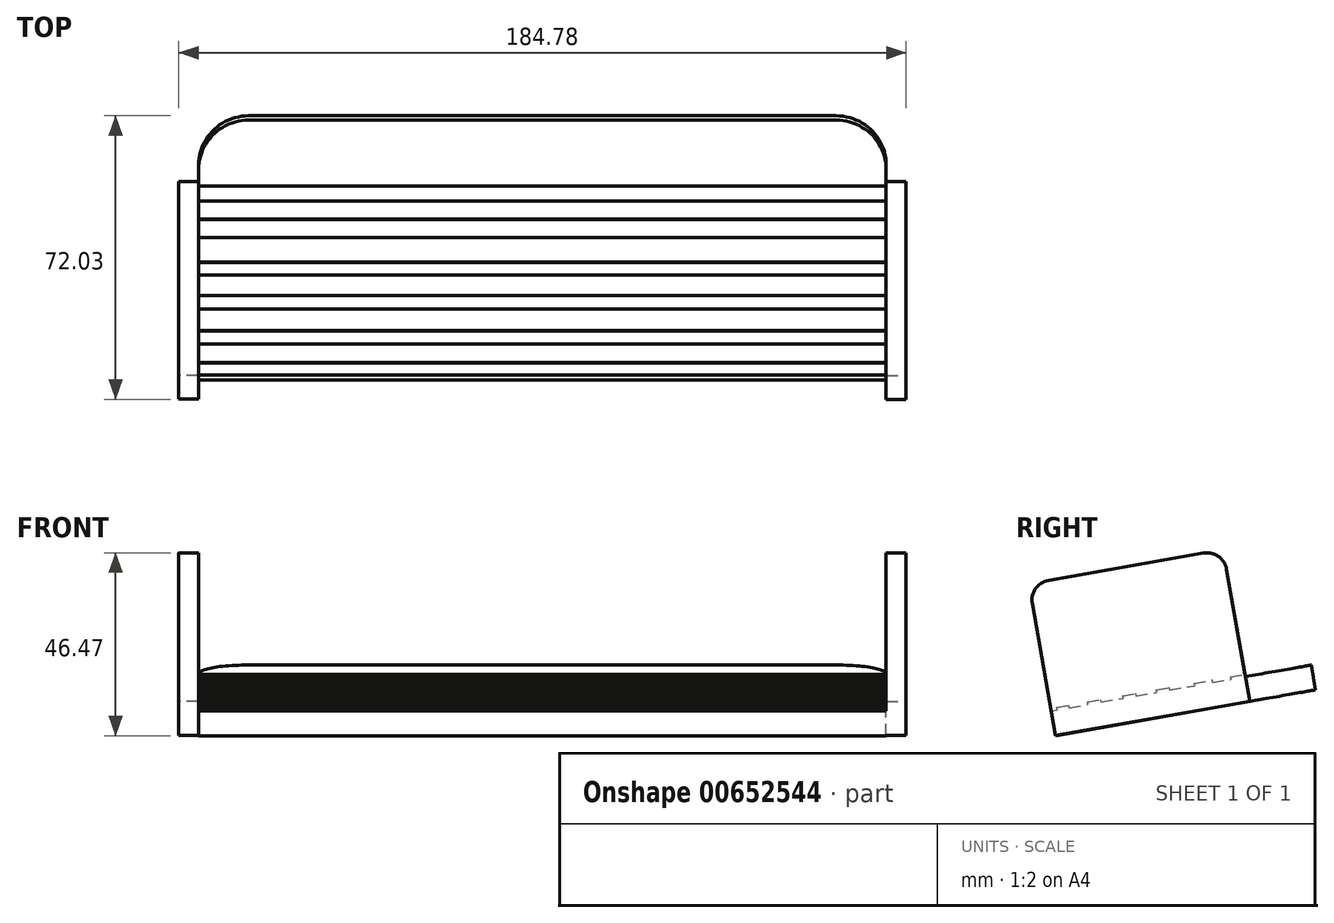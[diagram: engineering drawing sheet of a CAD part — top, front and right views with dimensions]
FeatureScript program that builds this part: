
annotation { "Feature Type Name" : "Feature", "Feature Type Description" : "" }
export const myFeature = defineFeature(function(context is Context, id is Id, definition is map)
    precondition{}
    {
        {
            var Q0;
            Q0=qCreatedBy(makeId("Front.planeOp"),FACE);
            var sketch = newSketch(context, id + "F0", { "sketchPlane" : qUnion([Q0])});
            skLineSegment(sketch, "E0.bottom", {"start": v(-82.9, 3.26) * mm, "end": v(91.78, 3.26) * mm});
            skLineSegment(sketch, "E0.top", {"start": v(-82.9, -3.13) * mm, "end": v(91.78, -3.13) * mm});
            skLineSegment(sketch, "E0.left", {"start": v(-82.9, 3.26) * mm, "end": v(-82.9, -3.13) * mm});
            skLineSegment(sketch, "E0.right", {"start": v(91.78, 3.26) * mm, "end": v(91.78, -3.13) * mm});
            skSolve(sketch);
        }
        {
            var Q0;
            Q0 = qSketchRegion(id + "F0", true);
            var Q1;
            Q1=sQuery(id+"F0.wireOp",EDGE,"E0.top");
            var Q2;
            Q2=sQuery(id+"F0.wireOp",EDGE,"E0.left");
            var Q3;
            Q3=sQuery(id+"F0.wireOp",EDGE,"E0.right");
            extrude(context, id + "F1", {"entities" : qUnion([Q0]), "surfaceEntities" : qUnion([Q1, Q2, Q3]), "depth" : 67.06 * mm, "offsetDistance" : 25.4 * mm});
        }
        {
            var Q0;
            Q0=makeQuery(id+"F1.opExtrude","CAP_EDGE",EDGE,{"disambiguationData":[OSD([sQuery(id+"F0.wireOp",EDGE,"E0.left")])],"isStart":true});
            var Q1;
            Q1=makeQuery(id+"F1.opExtrude","CAP_EDGE",EDGE,{"disambiguationData":[OSD([sQuery(id+"F0.wireOp",EDGE,"E0.right")])],"isStart":true});
            fillet(context, id + "F2", {"entities" : qUnion([Q0, Q1]), "radius" : 12.7 * mm, "tangentPropagation" : true, "allowEdgeOverflow" : false});
        }
        {
            var Q0;
            Q0=makeQuery(id+"F1.opExtrude","SWEPT_BODY",BODY,{"disambiguationData":[OSD([sQuery(id+"F0.wireOp",EDGE,"E0.bottom"),sQuery(id+"F0.wireOp",EDGE,"E0.top"),sQuery(id+"F0.wireOp",EDGE,"E0.left"),sQuery(id+"F0.wireOp",EDGE,"E0.right")])]});
            var Q1;
            Q1=makeQuery(id+"F1.opExtrude","CAP_EDGE",EDGE,{"disambiguationData":[OSD([sQuery(id+"F0.wireOp",EDGE,"E0.bottom")])],"isStart":true});
            transform(context, id + "F3", {"entities" : qUnion([Q0]), "transformType" : TransformType.ROTATION, "transformAxis" : qUnion([Q1]), "angle" : 10 * degree, "makeCopy" : false});
        }
        {
            var Q0;
            Q0=makeQuery(id+"F1.opExtrude","SWEPT_FACE",FACE,{"disambiguationData":[OSD([sQuery(id+"F0.wireOp",EDGE,"E0.bottom")])]});
            var sketch = newSketch(context, id + "F4", { "sketchPlane" : qUnion([Q0])});
            skLineSegment(sketch, "E1.bottom", {"start": v(-82.9, -65.03) * mm, "end": v(91.78, -65.03) * mm});
            skLineSegment(sketch, "E1.top", {"start": v(-82.9, -61.92) * mm, "end": v(91.78, -61.92) * mm});
            skLineSegment(sketch, "E1.left", {"start": v(-82.9, -65.03) * mm, "end": v(-82.9, -61.92) * mm});
            skLineSegment(sketch, "E1.right", {"start": v(91.78, -65.03) * mm, "end": v(91.78, -61.92) * mm});
            skLineSegment(sketch, "E2.bottom", {"start": v(-82.9, -57.1) * mm, "end": v(91.78, -57.1) * mm});
            skLineSegment(sketch, "E2.top", {"start": v(-82.9, -53.67) * mm, "end": v(91.78, -53.67) * mm});
            skLineSegment(sketch, "E2.left", {"start": v(-82.9, -57.1) * mm, "end": v(-82.9, -53.67) * mm});
            skLineSegment(sketch, "E2.right", {"start": v(91.78, -57.1) * mm, "end": v(91.78, -53.67) * mm});
            skLineSegment(sketch, "E3.bottom", {"start": v(-82.9, -48.06) * mm, "end": v(91.78, -48.06) * mm});
            skLineSegment(sketch, "E3.top", {"start": v(-82.9, -44.61) * mm, "end": v(91.78, -44.61) * mm});
            skLineSegment(sketch, "E3.left", {"start": v(-82.9, -48.06) * mm, "end": v(-82.9, -44.61) * mm});
            skLineSegment(sketch, "E3.right", {"start": v(91.78, -48.06) * mm, "end": v(91.78, -44.61) * mm});
            skLineSegment(sketch, "E4.bottom", {"start": v(-82.9, -39.31) * mm, "end": v(91.78, -39.31) * mm});
            skLineSegment(sketch, "E4.top", {"start": v(-82.9, -36.02) * mm, "end": v(91.78, -36.02) * mm});
            skLineSegment(sketch, "E4.left", {"start": v(-82.9, -39.31) * mm, "end": v(-82.9, -36.02) * mm});
            skLineSegment(sketch, "E4.right", {"start": v(91.78, -39.31) * mm, "end": v(91.78, -36.02) * mm});
            skLineSegment(sketch, "E5.bottom", {"start": v(-82.9, -29.61) * mm, "end": v(91.78, -29.61) * mm});
            skLineSegment(sketch, "E5.top", {"start": v(-82.9, -24.95) * mm, "end": v(91.78, -24.95) * mm});
            skLineSegment(sketch, "E5.left", {"start": v(-82.9, -29.61) * mm, "end": v(-82.9, -24.95) * mm});
            skLineSegment(sketch, "E5.right", {"start": v(91.78, -29.61) * mm, "end": v(91.78, -24.95) * mm});
            skLineSegment(sketch, "E6.bottom", {"start": v(-82.9, -20.2) * mm, "end": v(91.78, -20.2) * mm});
            skLineSegment(sketch, "E6.top", {"start": v(-82.9, -16.37) * mm, "end": v(91.78, -16.37) * mm});
            skLineSegment(sketch, "E6.left", {"start": v(-82.9, -20.2) * mm, "end": v(-82.9, -16.37) * mm});
            skLineSegment(sketch, "E6.right", {"start": v(91.78, -20.2) * mm, "end": v(91.78, -16.37) * mm});
            skPoint(sketch, "E7.oppositeSnap0", {"position": v(-79.18, -3.15) * mm});
            skLineSegment(sketch, "E8.left", {"start": v(91.78, -66.49) * mm, "end": v(91.78, -9.05) * mm});
            skLineSegment(sketch, "E9.bottom", {"start": v(-82.9, -16.37) * mm, "end": v(-87.97, -16.37) * mm});
            skLineSegment(sketch, "E9.top", {"start": v(-82.9, -66.44) * mm, "end": v(-87.97, -66.44) * mm});
            skLineSegment(sketch, "E9.left", {"start": v(-82.9, -16.37) * mm, "end": v(-82.9, -66.44) * mm});
            skLineSegment(sketch, "E9.right", {"start": v(-87.97, -16.37) * mm, "end": v(-87.97, -66.44) * mm});
            skLineSegment(sketch, "E10.bottom", {"start": v(91.78, -66.49) * mm, "end": v(96.81, -66.49) * mm});
            skLineSegment(sketch, "E10.top", {"start": v(91.78, -16.37) * mm, "end": v(96.81, -16.37) * mm});
            skLineSegment(sketch, "E10.left", {"start": v(91.78, -66.49) * mm, "end": v(91.78, -16.37) * mm});
            skLineSegment(sketch, "E10.right", {"start": v(96.81, -66.49) * mm, "end": v(96.81, -16.37) * mm});
            skSolve(sketch);
        }
        {
            var Q0;
            Q0=makeQuery(id+"F4.imprint","IMPRINT",FACE,{"disambiguationData":[TD([[makeQuery(id+"F4.imprint","IMPRINT",EDGE,{"derivedFrom":sQuery(id+"F4.wireOp",EDGE,"E6.bottom")}),1.0]])]});
            var Q1;
            Q1=makeQuery(id+"F4.imprint","IMPRINT",FACE,{"disambiguationData":[TD([[makeQuery(id+"F4.imprint","IMPRINT",EDGE,{"derivedFrom":sQuery(id+"F4.wireOp",EDGE,"E4.bottom")}),1.0]])]});
            var Q2;
            Q2=makeQuery(id+"F4.imprint","IMPRINT",FACE,{"disambiguationData":[TD([[makeQuery(id+"F4.imprint","IMPRINT",EDGE,{"derivedFrom":sQuery(id+"F4.wireOp",EDGE,"E5.bottom")}),1.0]])]});
            var Q3;
            Q3=makeQuery(id+"F4.imprint","IMPRINT",FACE,{"disambiguationData":[TD([[makeQuery(id+"F4.imprint","IMPRINT",EDGE,{"derivedFrom":sQuery(id+"F4.wireOp",EDGE,"E3.bottom")}),1.0]])]});
            var Q4;
            Q4=makeQuery(id+"F4.imprint","IMPRINT",FACE,{"disambiguationData":[TD([[makeQuery(id+"F4.imprint","IMPRINT",EDGE,{"derivedFrom":sQuery(id+"F4.wireOp",EDGE,"E2.bottom")}),1.0]])]});
            var Q5;
            Q5=makeQuery(id+"F4.imprint","IMPRINT",FACE,{"disambiguationData":[TD([[makeQuery(id+"F4.imprint","IMPRINT",EDGE,{"derivedFrom":sQuery(id+"F4.wireOp",EDGE,"E1.bottom")}),1.0]])]});
            extrude(context, id + "F5", {"entities" : qUnion([Q0, Q1, Q2, Q3, Q4, Q5]), "operationType" : NewBodyOperationType.ADD, "depth" : 0.64 * mm, "offsetDistance" : 25.4 * mm});
        }
        {
            var Q0;
            {var subQ8=sQuery(id+"F4.wireOp",EDGE,"E9.bottom");Q0=makeQuery(id+"F4.imprint","IMPRINT",FACE,{"disambiguationData":[TD([[makeQuery(id+"F4.imprint","IMPRINT",EDGE,{"derivedFrom":subQ8}),1.0]])]});}
            var Q1;
            {var subQ8=sQuery(id+"F4.wireOp",EDGE,"E10.bottom");Q1=makeQuery(id+"F4.imprint","IMPRINT",FACE,{"disambiguationData":[TD([[makeQuery(id+"F4.imprint","IMPRINT",EDGE,{"derivedFrom":subQ8}),1.0]])]});}
            extrude(context, id + "F6", {"entities" : qUnion([Q0, Q1]), "operationType" : NewBodyOperationType.ADD, "depth" : 32.77 * mm, "offsetDistance" : 25.4 * mm, "hasSecondDirection" : true, "secondDirectionOppositeDirection" : true, "secondDirectionDepth" : 6.35 * mm});
        }
        {
            var Q0;
            Q0=makeQuery(id+"F6.opExtrude","CAP_EDGE",EDGE,{"disambiguationData":[OSD([sQuery(id+"F4.wireOp",EDGE,"E10.top")])],"isStart":false});
            var Q1;
            Q1=makeQuery(id+"F6.opExtrude","CAP_EDGE",EDGE,{"disambiguationData":[OSD([sQuery(id+"F4.wireOp",EDGE,"E9.bottom")])],"isStart":false});
            var Q2;
            Q2=makeQuery(id+"F6.opExtrude","CAP_EDGE",EDGE,{"disambiguationData":[OSD([sQuery(id+"F4.wireOp",EDGE,"E9.top")])],"isStart":false});
            var Q3;
            Q3=makeQuery(id+"F6.opExtrude","CAP_EDGE",EDGE,{"disambiguationData":[OSD([sQuery(id+"F4.wireOp",EDGE,"E10.bottom")])],"isStart":false});
            fillet(context, id + "F7", {"entities" : qUnion([Q0, Q1, Q2, Q3]), "radius" : 5.08 * mm, "tangentPropagation" : true, "allowEdgeOverflow" : false});
        }
    });
